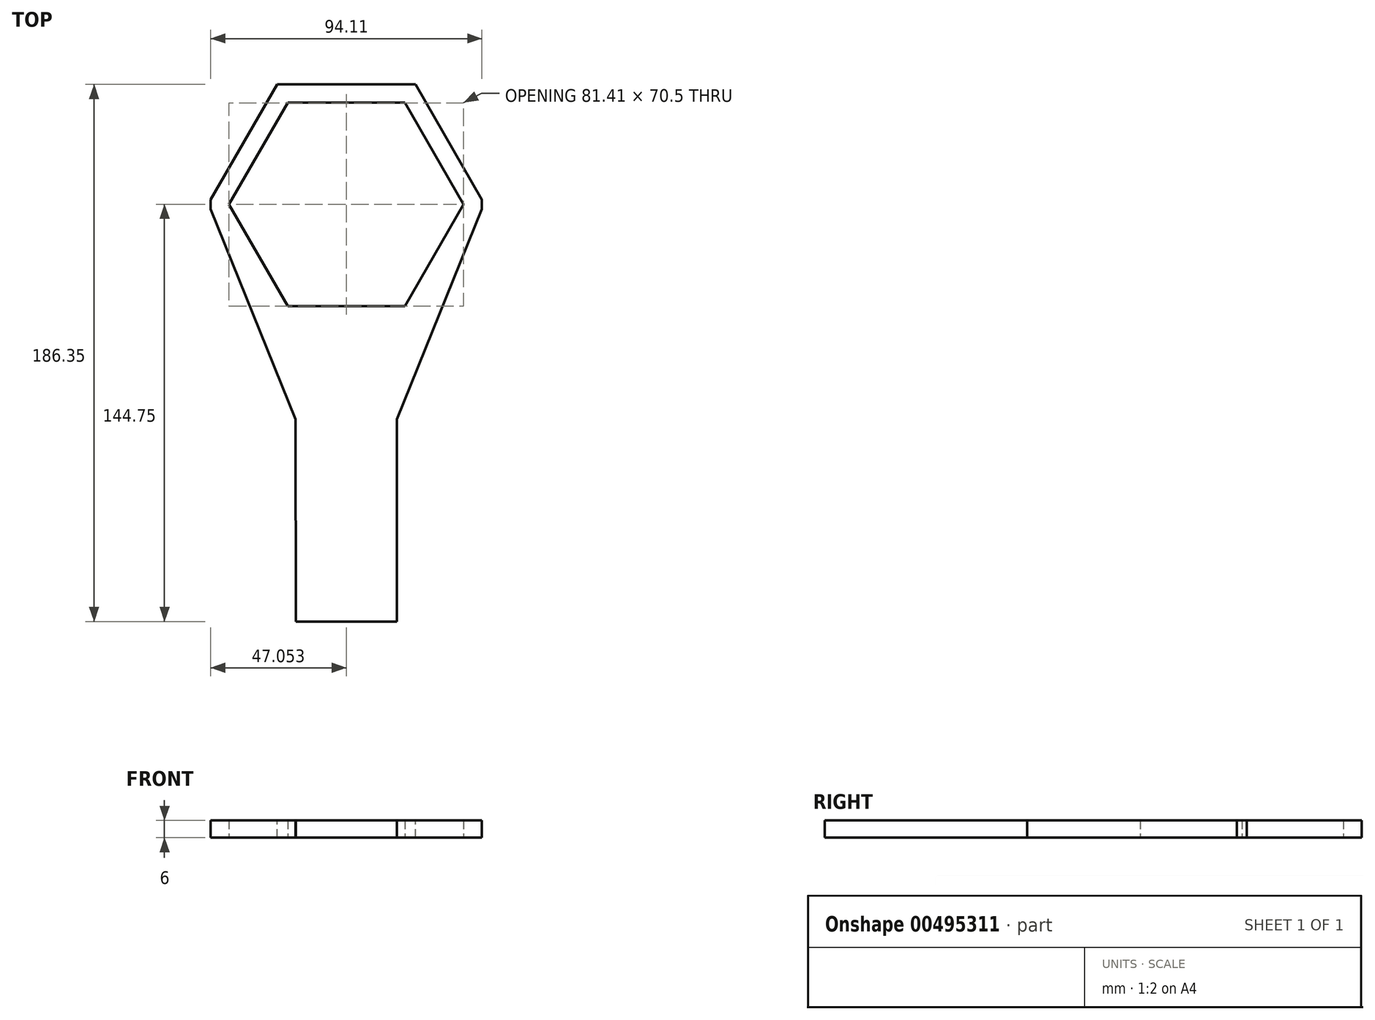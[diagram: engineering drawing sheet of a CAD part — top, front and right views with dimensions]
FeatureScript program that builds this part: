
annotation { "Feature Type Name" : "Feature", "Feature Type Description" : "" }
export const myFeature = defineFeature(function(context is Context, id is Id, definition is map)
    precondition{}
    {
        {
            var Q0;
            Q0=qCreatedBy(makeId("Top.planeOp"),FACE);
            var sketch = newSketch(context, id + "F0", { "sketchPlane" : qUnion([Q0])});
            skLineSegment(sketch, "E0.bottom", {"start": v(0, 0) * mm, "end": v(94.1, 0) * mm});
            skLineSegment(sketch, "E0.top", {"start": v(0, 83.2) * mm, "end": v(94.1, 83.2) * mm});
            skLineSegment(sketch, "E0.left", {"start": v(0, 0) * mm, "end": v(0, 83.2) * mm});
            skLineSegment(sketch, "E0.right", {"start": v(94.1, 0) * mm, "end": v(94.1, 83.2) * mm});
            skCircle(sketch, "E1.cCircle", {"center": v(47.05, 41.6) * mm, "radius": 35.25 * mm, "construction": true});
            skLineSegment(sketch, "E1.0", {"start": v(26.7, 6.35) * mm, "end": v(6.35, 41.6) * mm});
            skLineSegment(sketch, "E1.1", {"start": v(6.35, 41.6) * mm, "end": v(26.7, 76.85) * mm});
            skLineSegment(sketch, "E1.2", {"start": v(26.7, 76.85) * mm, "end": v(67.4, 76.85) * mm});
            skLineSegment(sketch, "E1.3", {"start": v(67.4, 76.85) * mm, "end": v(87.76, 41.6) * mm});
            skLineSegment(sketch, "E1.4", {"start": v(87.76, 41.6) * mm, "end": v(67.4, 6.35) * mm});
            skLineSegment(sketch, "E1.5", {"start": v(67.4, 6.35) * mm, "end": v(26.7, 6.35) * mm});
            skPoint(sketch, "E1.0.midPoint", {"position": v(16.53, 23.97) * mm});
            skLineSegment(sketch, "E2", {"start": v(47.05, 83.2) * mm, "end": v(47.05, 0) * mm, "construction": true});
            skSolve(sketch);
        }
        {
            var Q0;
            Q0=makeQuery(id+"F0.imprint","IMPRINT",FACE,{"disambiguationData":[TD([[makeQuery(id+"F0.imprint","IMPRINT",EDGE,{"derivedFrom":sQuery(id+"F0.wireOp",EDGE,"E0.bottom")}),1.0]])]});
            extrude(context, id + "F1", {"entities" : qUnion([Q0]), "depth" : 6 * mm});
        }
        {
            var Q0;
            Q0=makeQuery(id+"F1.opExtrude","CAP_FACE",FACE,{"disambiguationData":[OSD([sQuery(id+"F0.wireOp",EDGE,"E0.bottom"),sQuery(id+"F0.wireOp",EDGE,"E0.top"),sQuery(id+"F0.wireOp",EDGE,"E0.left"),sQuery(id+"F0.wireOp",EDGE,"E0.right"),sQuery(id+"F0.wireOp",EDGE,"E1.0"),sQuery(id+"F0.wireOp",EDGE,"E1.1"),sQuery(id+"F0.wireOp",EDGE,"E1.2"),sQuery(id+"F0.wireOp",EDGE,"E1.3"),sQuery(id+"F0.wireOp",EDGE,"E1.4"),sQuery(id+"F0.wireOp",EDGE,"E1.5")])],"isStart":false});
            var sketch = newSketch(context, id + "F2", { "sketchPlane" : qUnion([Q0])});
            skLineSegment(sketch, "E3", {"start": v(0, 43.3) * mm, "end": v(23.04, 83.2) * mm});
            skLineSegment(sketch, "E4", {"start": v(71.07, 83.2) * mm, "end": v(94.1, 43.3) * mm});
            skLineSegment(sketch, "E5", {"start": v(71.07, 0) * mm, "end": v(94.1, 39.9) * mm});
            skLineSegment(sketch, "E6", {"start": v(94.1, 39.9) * mm, "end": v(94.1, 0) * mm});
            skLineSegment(sketch, "E7", {"start": v(94.1, 0) * mm, "end": v(71.07, 0) * mm});
            skLineSegment(sketch, "E8", {"start": v(0, 0) * mm, "end": v(0, 39.9) * mm});
            skLineSegment(sketch, "E9", {"start": v(0, 39.9) * mm, "end": v(23.04, 0) * mm});
            skLineSegment(sketch, "E10", {"start": v(23.04, 0) * mm, "end": v(0, 0) * mm});
            skLineSegment(sketch, "E11", {"start": v(0, 43.3) * mm, "end": v(0, 83.2) * mm});
            skLineSegment(sketch, "E12", {"start": v(0, 83.2) * mm, "end": v(23.04, 83.2) * mm});
            skLineSegment(sketch, "E13", {"start": v(71.07, 83.2) * mm, "end": v(94.1, 83.2) * mm});
            skLineSegment(sketch, "E14", {"start": v(94.1, 83.2) * mm, "end": v(94.1, 43.3) * mm});
            skSolve(sketch);
        }
        {
            var Q0;
            Q0=makeQuery(id+"F2.imprint","IMPRINT",FACE,{"disambiguationData":[TD([[makeQuery(id+"F2.imprint","IMPRINT",EDGE,{"derivedFrom":sQuery(id+"F2.wireOp",EDGE,"E3")}),1.0]])]});
            var Q1;
            Q1=makeQuery(id+"F2.imprint","IMPRINT",FACE,{"disambiguationData":[TD([[makeQuery(id+"F2.imprint","IMPRINT",EDGE,{"derivedFrom":sQuery(id+"F2.wireOp",EDGE,"E4")}),1.0]])]});
            var Q2;
            Q2=makeQuery(id+"F2.imprint","IMPRINT",FACE,{"disambiguationData":[TD([[makeQuery(id+"F2.imprint","IMPRINT",EDGE,{"derivedFrom":sQuery(id+"F2.wireOp",EDGE,"E5")}),-1.0]])]});
            var Q3;
            Q3=makeQuery(id+"F2.imprint","IMPRINT",FACE,{"disambiguationData":[TD([[makeQuery(id+"F2.imprint","IMPRINT",EDGE,{"derivedFrom":sQuery(id+"F2.wireOp",EDGE,"E8")}),-1.0]])]});
            extrude(context, id + "F3", {"entities" : qUnion([Q0, Q1, Q2, Q3]), "operationType" : NewBodyOperationType.REMOVE, "endBound" : BoundingType.THROUGH_ALL, "oppositeDirection" : true, "depth" : 25.4 * mm});
        }
        {
            var Q0;
            Q0=makeQuery(id+"F1.opExtrude","CAP_FACE",FACE,{"disambiguationData":[OSD([sQuery(id+"F0.wireOp",EDGE,"E0.bottom"),sQuery(id+"F0.wireOp",EDGE,"E0.top"),sQuery(id+"F0.wireOp",EDGE,"E0.left"),sQuery(id+"F0.wireOp",EDGE,"E0.right"),sQuery(id+"F0.wireOp",EDGE,"E1.0"),sQuery(id+"F0.wireOp",EDGE,"E1.1"),sQuery(id+"F0.wireOp",EDGE,"E1.2"),sQuery(id+"F0.wireOp",EDGE,"E1.3"),sQuery(id+"F0.wireOp",EDGE,"E1.4"),sQuery(id+"F0.wireOp",EDGE,"E1.5")])],"isStart":false});
            var sketch = newSketch(context, id + "F4", { "sketchPlane" : qUnion([Q0])});
            skLineSegment(sketch, "E15", {"start": v(0, 39.9) * mm, "end": v(29.45, -32.99) * mm});
            skLineSegment(sketch, "E16", {"start": v(47.05, 76.85) * mm, "end": v(47.05, -103.15) * mm, "construction": true});
            skLineSegment(sketch, "E17", {"start": v(29.55, -103.15) * mm, "end": v(64.55, -103.15) * mm});
            skLineSegment(sketch, "E18", {"start": v(94.1, 39.9) * mm, "end": v(64.66, -32.99) * mm});
            skLineSegment(sketch, "E19", {"start": v(64.66, -32.99) * mm, "end": v(64.55, -103.15) * mm});
            skLineSegment(sketch, "E20", {"start": v(29.45, -32.99) * mm, "end": v(29.55, -103.15) * mm});
            skLineSegment(sketch, "E21", {"start": v(0, 39.9) * mm, "end": v(23.04, 0) * mm});
            skLineSegment(sketch, "E22", {"start": v(23.04, 0) * mm, "end": v(71.07, 0) * mm});
            skSolve(sketch);
        }
        {
            var Q0;
            Q0=makeQuery(id+"F4.imprint","IMPRINT",FACE,{"disambiguationData":[TD([[makeQuery(id+"F4.imprint","IMPRINT",EDGE,{"derivedFrom":sQuery(id+"F4.wireOp",EDGE,"E15")}),1.0]])]});
            extrude(context, id + "F5", {"entities" : qUnion([Q0]), "operationType" : NewBodyOperationType.ADD, "oppositeDirection" : true, "depth" : 6 * mm});
        }
    });
